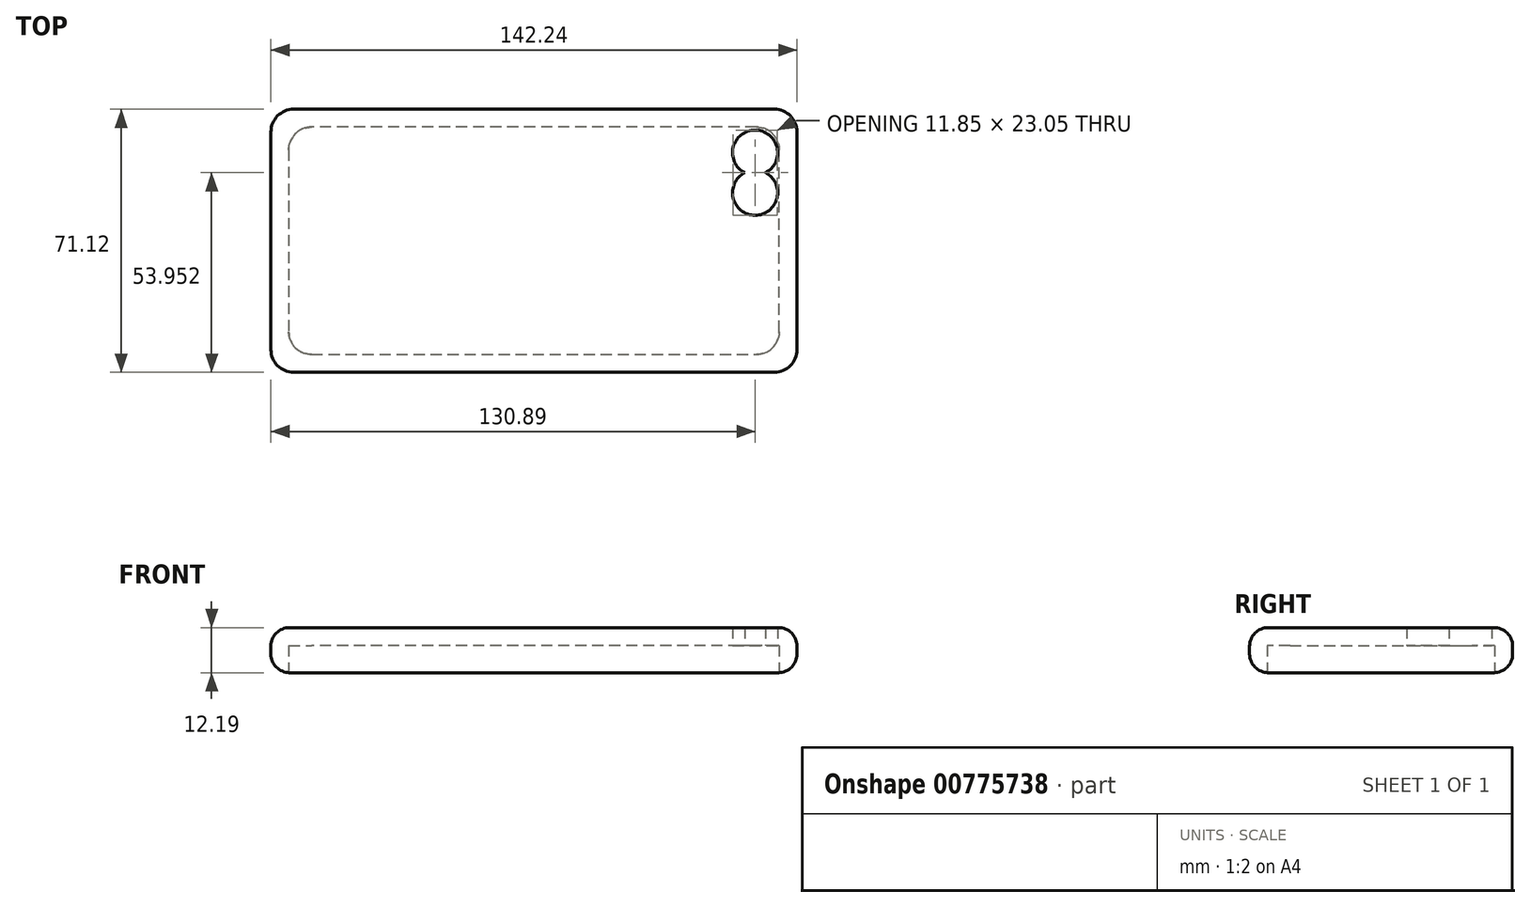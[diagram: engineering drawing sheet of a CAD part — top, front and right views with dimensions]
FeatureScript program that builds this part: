
annotation { "Feature Type Name" : "Feature", "Feature Type Description" : "" }
export const myFeature = defineFeature(function(context is Context, id is Id, definition is map)
    precondition{}
    {
        {
            var Q0;
            Q0=qCreatedBy(makeId("Top.planeOp"),FACE);
            var sketch = newSketch(context, id + "F0", { "sketchPlane" : qUnion([Q0])});
            skLineSegment(sketch, "E0.bottom", {"start": v(71.12, -35.56) * mm, "end": v(-71.12, -35.56) * mm});
            skLineSegment(sketch, "E0.top", {"start": v(71.12, 35.56) * mm, "end": v(-71.12, 35.56) * mm});
            skLineSegment(sketch, "E0.left", {"start": v(71.12, -35.56) * mm, "end": v(71.12, 35.56) * mm});
            skLineSegment(sketch, "E0.right", {"start": v(-71.12, -35.56) * mm, "end": v(-71.12, 35.56) * mm});
            skPoint(sketch, "E0.middle", {"position": v(0, 0) * mm});
            skSolve(sketch);
        }
        {
            var Q0;
            {var subQ12=sQuery(id+"F0.wireOp",EDGE,"E0.top");Q0=makeQuery(id+"F0.imprint","IMPRINT",FACE,{"disambiguationData":[TD([[makeQuery(id+"F0.imprint","IMPRINT",EDGE,{"derivedFrom":subQ12}),1.0]])]});}
            var Q1;
            {var subQ0=sQuery(id+"F0.wireOp",EDGE,"v6TGKBHT-TTCF-ISge-G5St-gdAdDseLC5ZP");Q1=makeQuery(id+"F0.imprint","IMPRINT",FACE,{"disambiguationData":[TD([[makeQuery(id+"F0.imprint","IMPRINT",EDGE,{"derivedFrom":subQ0}),1.0]])]});}
            extrude(context, id + "F1", {"entities" : qUnion([Q0, Q1]), "depth" : 12.2 * mm, "offsetDistance" : 25.4 * mm});
        }
        {
            var Q0;
            Q0=qCreatedBy(makeId("Top.planeOp"),FACE);
            var sketch = newSketch(context, id + "F2", { "sketchPlane" : qUnion([Q0])});
            skCircle(sketch, "E1", {"center": v(59.77, 23.82) * mm, "radius": 7.24 * mm});
            skCircle(sketch, "E2", {"center": v(59.77, 12.97) * mm, "radius": 7.24 * mm});
            skLineSegment(sketch, "E3", {"start": v(59.77, 23.82) * mm, "end": v(59.77, 16.58) * mm});
            skLineSegment(sketch, "E4", {"start": v(59.77, 16.58) * mm, "end": v(59.77, 31.06) * mm});
            skLineSegment(sketch, "E5", {"start": v(59.77, 23.82) * mm, "end": v(67, 23.82) * mm});
            skLineSegment(sketch, "E6", {"start": v(67, 23.82) * mm, "end": v(52.53, 23.82) * mm});
            skLineSegment(sketch, "E7", {"start": v(59.77, 31.1) * mm, "end": v(59.77, 5.7) * mm});
            skLineSegment(sketch, "E8", {"start": v(67, 23.82) * mm, "end": v(67, 12.97) * mm});
            skLineSegment(sketch, "E9", {"start": v(52.53, 23.82) * mm, "end": v(52.53, 12.97) * mm});
            skSolve(sketch);
        }
        {
            var Q0;
            Q0=makeQuery(id+"F1.opExtrude","CAP_FACE",FACE,{"disambiguationData":[OSD([sQuery(id+"F0.wireOp",EDGE,"E0.bottom"),sQuery(id+"F0.wireOp",EDGE,"E0.top"),sQuery(id+"F0.wireOp",EDGE,"E0.left"),sQuery(id+"F0.wireOp",EDGE,"E0.right"),sQuery(id+"F0.wireOp",EDGE,"LqsHU5QW-Zjdh-RZ9M-po5b-BVYqEDW1c5YE"),sQuery(id+"F0.wireOp",EDGE,"09rxOdGG-L81P-ENHM-nMKE-CuDwEdNW0GXP"),sQuery(id+"F0.wireOp",EDGE,"5lGGLe0o-o5I0-ylhx-0gj0-kNQQUklSdgO7"),sQuery(id+"F0.wireOp",EDGE,"oa7pL8GJ-TQ6d-zuGW-lpXq-MlO6gROTHeYA")])],"isStart":true});
            shell(context, id + "F3", {"entities" : qUnion([Q0]), "thickness" : 4.83 * mm});
        }
        {
            var Q0;
            Q0=sQuery(id+"F2.wireOp",VERTEX,"E2.center");
            var Q1;
            Q1=sQuery(id+"F2.wireOp",VERTEX,"E3.start");
            var Q2;
            Q2=makeQuery(id+"F1.opExtrude","SWEPT_BODY",BODY,{"disambiguationData":[OSD([sQuery(id+"F0.wireOp",EDGE,"E0.bottom"),sQuery(id+"F0.wireOp",EDGE,"E0.top"),sQuery(id+"F0.wireOp",EDGE,"E0.left"),sQuery(id+"F0.wireOp",EDGE,"E0.right")])]});
            hole(context, id + "F4", {"style" : HoleStyle.SIMPLE, "endStyle" : HoleEndStyle.THROUGH, "oppositeDirection" : true, "holeDiameter" : 12.2 * mm, "majorDiameter" : 6.35 * mm, "isTappedThrough" : true, "tappedDepth" : 12.7 * mm, "tapClearance" : 3, "locations" : qUnion([Q0, Q1]), "scope" : qUnion([Q2])});
        }
        {
            var Q0;
            Q0=makeQuery(id+"F3.opShell","OFFSET_EDGE",EDGE,{"disambiguationData":[OSD([sQuery(id+"F0.wireOp",EDGE,"E0.bottom"),sQuery(id+"F0.wireOp",EDGE,"E0.left")])]});
            var Q1;
            Q1=makeQuery(id+"F3.opShell","OFFSET_EDGE",EDGE,{"disambiguationData":[OSD([sQuery(id+"F0.wireOp",EDGE,"E0.top"),sQuery(id+"F0.wireOp",EDGE,"E0.left")])]});
            var Q2;
            Q2=makeQuery(id+"F3.opShell","OFFSET_EDGE",EDGE,{"disambiguationData":[OSD([sQuery(id+"F0.wireOp",EDGE,"E0.top"),sQuery(id+"F0.wireOp",EDGE,"E0.right")])]});
            var Q3;
            Q3=makeQuery(id+"F3.opShell","OFFSET_EDGE",EDGE,{"disambiguationData":[OSD([sQuery(id+"F0.wireOp",EDGE,"E0.bottom"),sQuery(id+"F0.wireOp",EDGE,"E0.right")])]});
            var Q4;
            Q4=makeQuery(id+"F1.opExtrude","SWEPT_EDGE",EDGE,{"disambiguationData":[OSD([sQuery(id+"F0.wireOp",EDGE,"E0.top"),sQuery(id+"F0.wireOp",EDGE,"E0.right")])]});
            var Q5;
            Q5=makeQuery(id+"F1.opExtrude","SWEPT_EDGE",EDGE,{"disambiguationData":[OSD([sQuery(id+"F0.wireOp",EDGE,"E0.bottom"),sQuery(id+"F0.wireOp",EDGE,"E0.right")])]});
            var Q6;
            Q6=makeQuery(id+"F1.opExtrude","SWEPT_EDGE",EDGE,{"disambiguationData":[OSD([sQuery(id+"F0.wireOp",EDGE,"E0.bottom"),sQuery(id+"F0.wireOp",EDGE,"E0.left")])]});
            var Q7;
            Q7=makeQuery(id+"F1.opExtrude","SWEPT_EDGE",EDGE,{"disambiguationData":[OSD([sQuery(id+"F0.wireOp",EDGE,"E0.top"),sQuery(id+"F0.wireOp",EDGE,"E0.left")])]});
            fillet(context, id + "F5", {"entities" : qUnion([Q0, Q1, Q2, Q3, Q4, Q5, Q6, Q7]), "radius" : 6.15 * mm, "tangentPropagation" : true, "allowEdgeOverflow" : false});
        }
        {
            var Q0;
            Q0=makeQuery(id+"F1.opExtrude","CAP_EDGE",EDGE,{"disambiguationData":[OSD([sQuery(id+"F0.wireOp",EDGE,"E0.top")])],"isStart":true});
            fillet(context, id + "F6", {"entities" : qUnion([Q0]), "radius" : 5.08 * mm, "tangentPropagation" : true, "allowEdgeOverflow" : false});
        }
        {
            var Q0;
            Q0=makeQuery(id+"F1.opExtrude","CAP_EDGE",EDGE,{"disambiguationData":[OSD([sQuery(id+"F0.wireOp",EDGE,"E0.top")])],"isStart":false});
            fillet(context, id + "F7", {"entities" : qUnion([Q0]), "radius" : 5.08 * mm, "tangentPropagation" : true, "allowEdgeOverflow" : false});
        }
    });
